# Revit family: S-tank_AT
name_source: partatom
category: Оборудование
units: mm (PartAtom-declared; Revit-internal decimal feet)

## family parameters
Всегда вертикально = Да
Классификация = Нет
На основе рабочей плоскости = Нет
Общий = Нет
При загрузке вырезать с полостями = Нет
Размер круглого соединителя = Использовать диаметр
Тип детали = Нормальный
Точка расчета площади = Нет

## types (9) — shared parameters
ADSK_URL документации изделия = http://s-tank.ru
ADSK_Группирование = Оборудование
ADSK_Единица измерения = шт.
ADSK_Завод-изготовитель = ООО “С-ТЭНК ВОТЕР ХИТЕРС”
ADSK_Наименование = Буферная емкость
DN1 = 40 мм
DN2 = 15 мм
shrf = 18 мм
Разработка семейств = https://rubim.tech

## per-type parameters (varying)
| type | A | ADSK_Код изделия | ADSK_Марка | ADSK_Масса | ADSK_Обозначение | B | C | D | H | a | Диаметр |
| AT300 | 230 мм | 1.0001 | AT 300 | 65 | AT 300 | 600 мм | 970 мм | 1340 мм | 1600 мм | 105 мм | 630 мм |
| AT500 | 225 мм | 1.0002 | AT 500 | 87 | AT500 | 595 мм | 965 мм | 1335 мм | 1605 мм | 130 мм | 780 мм |
| AT750 | 215 мм | 1.0003 | AT 750 | 103 | AT750 | 585 мм | 955 мм | 1325 мм | 1630 мм | 153 мм | 920 мм |
| AT1000 | 205 мм | 1.0004 | AT 1000 | 131 | AT1000 | 775 мм | 1345 мм | 1915 мм | 2205 мм | 153 мм | 920 мм |
| AT1200 | 275 мм | 1.0005 | AT 1200 | 174 | AT1200 | 735 мм | 1195 мм | 1655 мм | 2080 мм | 178 мм | 1070 мм |
| AT1500 | 275 мм | 1.0006 | AT 1500 | 200 | AT1500 | 850 мм | 1425 мм | 2000 мм | 2370 мм | 178 мм | 1070 мм |
| AT2000 | 360 мм | 1.0007 | AT 2000 | 246 | AT2000 | 820 мм | 1280 мм | 1740 мм | 2100 мм | 225 мм | 1350 мм |
| AT3000 | 475 мм | 1.0008 | AT 3000 | 450 | AT3000 | 935 мм | 1395 мм | 1855 мм | 2315 мм | 272 мм | 1630 мм |
| AT5000 | 475 мм | 1.0009 | AT 5000 | 615 | AT5000 | 1185 мм | 1895 мм | 2605 мм | 2965 мм | 272 мм | 1630 мм |
